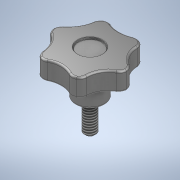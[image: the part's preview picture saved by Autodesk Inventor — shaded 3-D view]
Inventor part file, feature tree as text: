
AUTODESK INVENTOR PART (.ipt)
format: ipt  version: 2020 (Build 240168000, 168)  size: 724,992 bytes
history: mixed  units: in
note: dims shown in document units (in); Inventor stores cm internally (conversion verified against a paired STEP export)
features: extrude x1, chamfer x1, thread x1, sketch x1, other x1, fillet x1, imported_body x1
ambient origin geometry x8: Origin, YZ Plane, XZ Plane, XY Plane, X Axis, Y Axis, Z Axis, Center Point
bodies: Solid1 (imported_parasolid), Solid2 (imported_parasolid)
feature tree (7):
  extrude  "Extrusion1"  Depth=0.7874in TaperAngle=0.0deg
  chamfer  "Chamfer1"  Distance=0.0394in Angle=45.0deg
  thread  "Thread2"  [1 undecoded]
  sketch  "Sketch1"  dims[d2=0.25in d3=0.7874in d4=0.0in d5=0.0394in d6=0.0787in d7=45.0deg d8=0.748in d9=0.0in]
  other  "Cut-Extrude4"
  fillet  "Fillet8"  [1 undecoded]
  imported_body  NMx_Import_Brep_tag  [imported B-rep: ~11 faces, bbox_mm=None]
note: 2 required parameter values undecoded (feature->parameter linkage not recoverable at this tier; creation-order binding heuristic only, values carry confidence <= 0.55)
